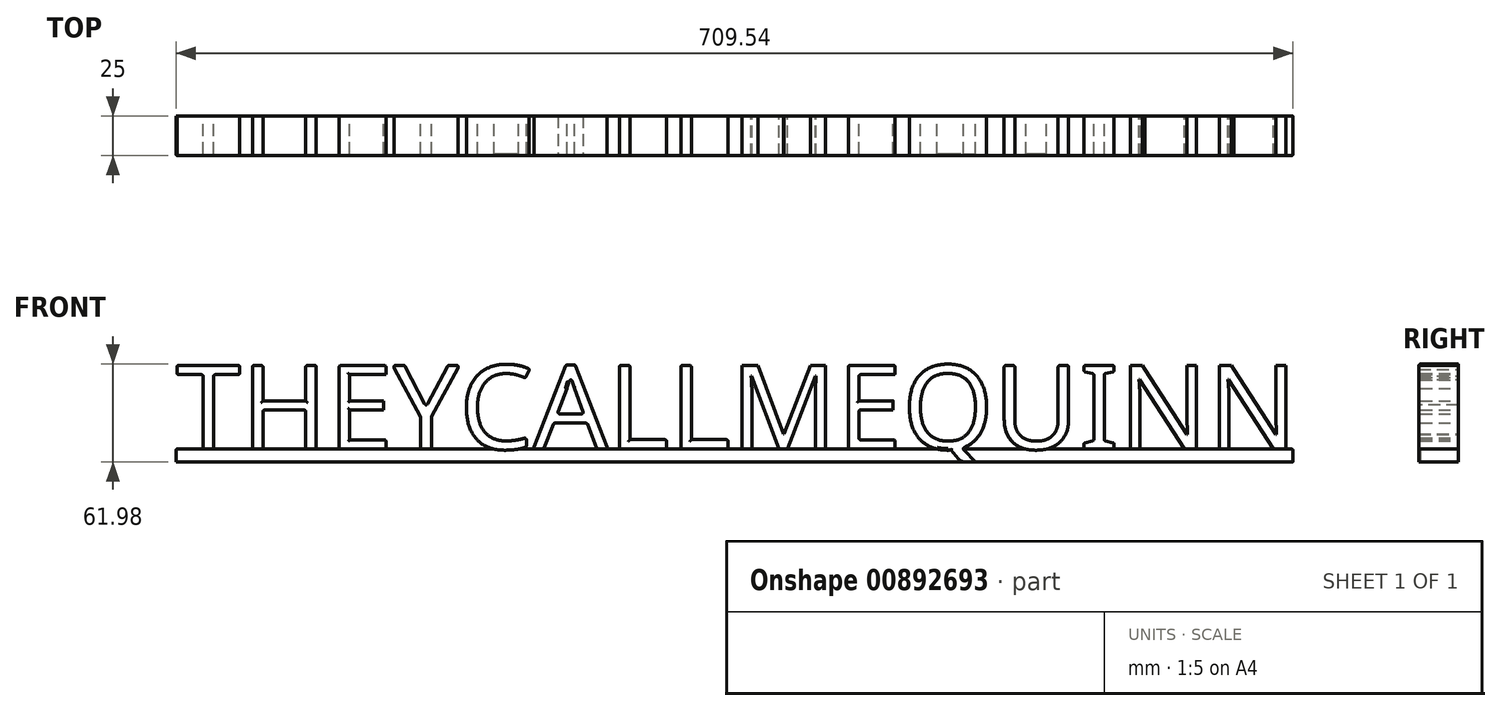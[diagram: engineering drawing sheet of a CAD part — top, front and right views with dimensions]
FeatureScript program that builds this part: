
annotation { "Feature Type Name" : "Feature", "Feature Type Description" : "" }
export const myFeature = defineFeature(function(context is Context, id is Id, definition is map)
    precondition{}
    {
        {
            var Q0;
            Q0=qCreatedBy(makeId("Front.planeOp"),FACE);
            var sketch = newSketch(context, id + "F0", { "sketchPlane" : qUnion([Q0])});
            skText(sketch, "E0", { "text": "THEYCALLMEQUINN", "fontName": "NotoSans-Regular.ttf"});
            skLineSegment(sketch, "E1.bottom", {"start": v(-74, 3.83) * mm, "end": v(635.54, 3.83) * mm});
            skLineSegment(sketch, "E1.top", {"start": v(-74, -4.21) * mm, "end": v(635.54, -4.21) * mm});
            skLineSegment(sketch, "E1.left", {"start": v(-74, 3.83) * mm, "end": v(-74, -4.21) * mm});
            skLineSegment(sketch, "E1.right", {"start": v(635.54, 3.83) * mm, "end": v(635.54, -4.21) * mm});
            const initialGuessF0  = {"E0": [-0.074, 0.00383, 1, 0, 0.05356]};
            skSetInitialGuess(sketch, initialGuessF0);
            skSolve(sketch);
        }
        {
            var Q0;
            {var subQ0=sQuery(id+"F0.wireOp",EDGE,"E0.sketch_text.stroke-1");Q0=makeQuery(id+"F0.imprint","IMPRINT",FACE,{"disambiguationData":[TD([[makeQuery(id+"F0.imprint","IMPRINT",EDGE,{"derivedFrom":subQ0}),-1.0]])]});}
            var Q1;
            {var subQ0=sQuery(id+"F0.wireOp",EDGE,"E0.sketch_text.stroke-21");Q1=makeQuery(id+"F0.imprint","IMPRINT",FACE,{"disambiguationData":[TD([[makeQuery(id+"F0.imprint","IMPRINT",EDGE,{"derivedFrom":subQ0}),-1.0]])]});}
            var Q2;
            Q2=makeQuery(id+"F0.imprint","IMPRINT",FACE,{"disambiguationData":[TD([[makeQuery(id+"F0.imprint","IMPRINT",EDGE,{"derivedFrom":sQuery(id+"F0.wireOp",EDGE,"E0.sketch_text.stroke-32")}),-1.0]])]});
            var Q3;
            Q3=makeQuery(id+"F0.imprint","IMPRINT",FACE,{"disambiguationData":[TD([[makeQuery(id+"F0.imprint","IMPRINT",EDGE,{"derivedFrom":sQuery(id+"F0.wireOp",EDGE,"E0.sketch_text.stroke-41")}),-1.0]])]});
            var Q4;
            {var subQ0=sQuery(id+"F0.wireOp",EDGE,"E0.sketch_text.stroke-70");Q4=makeQuery(id+"F0.imprint","IMPRINT",FACE,{"disambiguationData":[TD([[makeQuery(id+"F0.imprint","IMPRINT",EDGE,{"derivedFrom":subQ0}),-1.0]])]});}
            var Q5;
            {var subQ1=sQuery(id+"F0.wireOp",EDGE,"E0.sketch_text.stroke-76");Q5=makeQuery(id+"F0.imprint","IMPRINT",FACE,{"disambiguationData":[TD([[makeQuery(id+"F0.imprint","IMPRINT",EDGE,{"derivedFrom":subQ1}),-1.0]])]});}
            var Q6;
            {var subQ1=sQuery(id+"F0.wireOp",EDGE,"E0.sketch_text.stroke-101");Q6=makeQuery(id+"F0.imprint","IMPRINT",FACE,{"disambiguationData":[TD([[makeQuery(id+"F0.imprint","IMPRINT",EDGE,{"derivedFrom":subQ1}),-1.0]])]});}
            var Q7;
            Q7=makeQuery(id+"F0.imprint","IMPRINT",FACE,{"disambiguationData":[TD([[makeQuery(id+"F0.imprint","IMPRINT",EDGE,{"derivedFrom":sQuery(id+"F0.wireOp",EDGE,"E0.sketch_text.stroke-132")}),-1.0]])]});
            var Q8;
            {var subQ1=sQuery(id+"F0.wireOp",EDGE,"E0.sketch_text.stroke-147");Q8=makeQuery(id+"F0.imprint","IMPRINT",FACE,{"disambiguationData":[TD([[makeQuery(id+"F0.imprint","IMPRINT",EDGE,{"derivedFrom":subQ1}),-1.0]])]});}
            var Q9;
            {var subQ1=sQuery(id+"F0.wireOp",EDGE,"E0.sketch_text.stroke-9");Q9=makeQuery(id+"F0.imprint","IMPRINT",FACE,{"disambiguationData":[TD([[makeQuery(id+"F0.imprint","IMPRINT",EDGE,{"derivedFrom":subQ1}),-1.0]])]});}
            var Q10;
            {var subQ0=sQuery(id+"F0.wireOp",EDGE,"E0.sketch_text.stroke-48");Q10=makeQuery(id+"F0.imprint","IMPRINT",FACE,{"disambiguationData":[TD([[makeQuery(id+"F0.imprint","IMPRINT",EDGE,{"derivedFrom":subQ0}),-1.0]])]});}
            var Q11;
            Q11=makeQuery(id+"F0.imprint","IMPRINT",FACE,{"disambiguationData":[TD([[makeQuery(id+"F0.imprint","IMPRINT",EDGE,{"derivedFrom":sQuery(id+"F0.wireOp",EDGE,"E0.sketch_text.stroke-112")}),-1.0]])]});
            var Q12;
            {var subQ0=sQuery(id+"F0.wireOp",EDGE,"E0.sketch_text.stroke-135");var subQ1=sQuery(id+"F0.wireOp",EDGE,"E0.sketch_text.stroke-134");var subQ2=makeQuery(id+"F0.imprint","INTERSECT",VERTEX,{"derivedFrom":[subQ1,subQ0]});Q12=makeQuery(id+"F0.imprint","IMPRINT",FACE,{"disambiguationData":[TD([[makeQuery(id+"F0.imprint","IMPRINT",EDGE,{"disambiguationData":[TD([[subQ2,1.0]])],"derivedFrom":subQ1}),-1.0]])]});}
            var Q13;
            {var subQ2=sQuery(id+"F0.wireOp",EDGE,"E0.sketch_text.stroke-159");Q13=makeQuery(id+"F0.imprint","IMPRINT",FACE,{"disambiguationData":[TD([[makeQuery(id+"F0.imprint","IMPRINT",EDGE,{"derivedFrom":subQ2}),-1.0]])]});}
            var Q14;
            {var subQ3=sQuery(id+"F0.wireOp",EDGE,"E0.sketch_text.stroke-177");Q14=makeQuery(id+"F0.imprint","IMPRINT",FACE,{"disambiguationData":[TD([[makeQuery(id+"F0.imprint","IMPRINT",EDGE,{"derivedFrom":subQ3}),-1.0]])]});}
            var Q15;
            {var subQ1=sQuery(id+"F0.wireOp",EDGE,"E0.sketch_text.stroke-57");Q15=makeQuery(id+"F0.imprint","IMPRINT",FACE,{"disambiguationData":[TD([[makeQuery(id+"F0.imprint","IMPRINT",EDGE,{"derivedFrom":subQ1}),-1.0]])]});}
            var Q16;
            {var subQ1=sQuery(id+"F0.wireOp",EDGE,"E0.sketch_text.stroke-82");Q16=makeQuery(id+"F0.imprint","IMPRINT",FACE,{"disambiguationData":[TD([[makeQuery(id+"F0.imprint","IMPRINT",EDGE,{"derivedFrom":subQ1}),-1.0]])]});}
            var Q17;
            {var subQ1=sQuery(id+"F0.wireOp",EDGE,"E0.sketch_text.stroke-117");Q17=makeQuery(id+"F0.imprint","IMPRINT",FACE,{"disambiguationData":[TD([[makeQuery(id+"F0.imprint","IMPRINT",EDGE,{"derivedFrom":subQ1}),-1.0]])]});}
            extrude(context, id + "F1", {"entities" : qUnion([Q0, Q1, Q2, Q3, Q4, Q5, Q6, Q7, Q8, Q9, Q10, Q11, Q12, Q13, Q14, Q15, Q16, Q17]), "depth" : 25 * mm, "offsetDistance" : 25 * mm});
        }
        {
            var Q0;
            Q0=makeQuery(id+"F1.opExtrude","CAP_FACE",FACE,{"disambiguationData":[OSD([sQuery(id+"F0.wireOp",EDGE,"E0.sketch_text.stroke-1"),sQuery(id+"F0.wireOp",EDGE,"E0.sketch_text.stroke-2"),sQuery(id+"F0.wireOp",EDGE,"E0.sketch_text.stroke-3"),sQuery(id+"F0.wireOp",EDGE,"E0.sketch_text.stroke-4"),sQuery(id+"F0.wireOp",EDGE,"E0.sketch_text.stroke-5"),sQuery(id+"F0.wireOp",EDGE,"E0.sketch_text.stroke-6"),sQuery(id+"F0.wireOp",EDGE,"E0.sketch_text.stroke-7"),sQuery(id+"F0.wireOp",EDGE,"E1.bottom")])],"isStart":false});
            var Q1;
            Q1=makeQuery(id+"F1.opExtrude","CAP_FACE",FACE,{"disambiguationData":[OSD([sQuery(id+"F0.wireOp",EDGE,"E0.sketch_text.stroke-9"),sQuery(id+"F0.wireOp",EDGE,"E0.sketch_text.stroke-10"),sQuery(id+"F0.wireOp",EDGE,"E0.sketch_text.stroke-11"),sQuery(id+"F0.wireOp",EDGE,"E0.sketch_text.stroke-13"),sQuery(id+"F0.wireOp",EDGE,"E0.sketch_text.stroke-14"),sQuery(id+"F0.wireOp",EDGE,"E0.sketch_text.stroke-15"),sQuery(id+"F0.wireOp",EDGE,"E0.sketch_text.stroke-16"),sQuery(id+"F0.wireOp",EDGE,"E0.sketch_text.stroke-17"),sQuery(id+"F0.wireOp",EDGE,"E0.sketch_text.stroke-18"),sQuery(id+"F0.wireOp",EDGE,"E0.sketch_text.stroke-19"),sQuery(id+"F0.wireOp",EDGE,"E1.bottom")])],"isStart":false});
            var Q2;
            Q2=makeQuery(id+"F1.opExtrude","CAP_FACE",FACE,{"disambiguationData":[OSD([sQuery(id+"F0.wireOp",EDGE,"E0.sketch_text.stroke-21"),sQuery(id+"F0.wireOp",EDGE,"E0.sketch_text.stroke-22"),sQuery(id+"F0.wireOp",EDGE,"E0.sketch_text.stroke-23"),sQuery(id+"F0.wireOp",EDGE,"E0.sketch_text.stroke-24"),sQuery(id+"F0.wireOp",EDGE,"E0.sketch_text.stroke-25"),sQuery(id+"F0.wireOp",EDGE,"E0.sketch_text.stroke-26"),sQuery(id+"F0.wireOp",EDGE,"E0.sketch_text.stroke-27"),sQuery(id+"F0.wireOp",EDGE,"E0.sketch_text.stroke-28"),sQuery(id+"F0.wireOp",EDGE,"E0.sketch_text.stroke-29"),sQuery(id+"F0.wireOp",EDGE,"E0.sketch_text.stroke-30"),sQuery(id+"F0.wireOp",EDGE,"E0.sketch_text.stroke-31"),sQuery(id+"F0.wireOp",EDGE,"E1.bottom")])],"isStart":false});
            var Q3;
            Q3=makeQuery(id+"F1.opExtrude","CAP_FACE",FACE,{"disambiguationData":[OSD([sQuery(id+"F0.wireOp",EDGE,"E0.sketch_text.stroke-32"),sQuery(id+"F0.wireOp",EDGE,"E0.sketch_text.stroke-33"),sQuery(id+"F0.wireOp",EDGE,"E0.sketch_text.stroke-34"),sQuery(id+"F0.wireOp",EDGE,"E0.sketch_text.stroke-35"),sQuery(id+"F0.wireOp",EDGE,"E0.sketch_text.stroke-37"),sQuery(id+"F0.wireOp",EDGE,"E0.sketch_text.stroke-38"),sQuery(id+"F0.wireOp",EDGE,"E0.sketch_text.stroke-39"),sQuery(id+"F0.wireOp",EDGE,"E0.sketch_text.stroke-40"),sQuery(id+"F0.wireOp",EDGE,"E1.bottom")])],"isStart":false});
            var Q4;
            Q4=makeQuery(id+"F1.opExtrude","CAP_FACE",FACE,{"disambiguationData":[OSD([sQuery(id+"F0.wireOp",EDGE,"E0.sketch_text.stroke-41"),sQuery(id+"F0.wireOp",EDGE,"E0.sketch_text.stroke-42"),sQuery(id+"F0.wireOp",EDGE,"E0.sketch_text.stroke-43"),sQuery(id+"F0.wireOp",EDGE,"E0.sketch_text.stroke-44"),sQuery(id+"F0.wireOp",EDGE,"E0.sketch_text.stroke-45"),sQuery(id+"F0.wireOp",EDGE,"E0.sketch_text.stroke-46"),sQuery(id+"F0.wireOp",EDGE,"E0.sketch_text.stroke-47"),sQuery(id+"F0.wireOp",EDGE,"E0.sketch_text.stroke-48"),sQuery(id+"F0.wireOp",EDGE,"E0.sketch_text.stroke-49"),sQuery(id+"F0.wireOp",EDGE,"E0.sketch_text.stroke-50"),sQuery(id+"F0.wireOp",EDGE,"E0.sketch_text.stroke-51"),sQuery(id+"F0.wireOp",EDGE,"E0.sketch_text.stroke-52"),sQuery(id+"F0.wireOp",EDGE,"E0.sketch_text.stroke-53"),sQuery(id+"F0.wireOp",EDGE,"E0.sketch_text.stroke-54"),sQuery(id+"F0.wireOp",EDGE,"E0.sketch_text.stroke-55"),sQuery(id+"F0.wireOp",EDGE,"E0.sketch_text.stroke-56")])],"isStart":false});
            var Q5;
            Q5=makeQuery(id+"F1.opExtrude","CAP_FACE",FACE,{"disambiguationData":[OSD([sQuery(id+"F0.wireOp",EDGE,"E0.sketch_text.stroke-57"),sQuery(id+"F0.wireOp",EDGE,"E0.sketch_text.stroke-58"),sQuery(id+"F0.wireOp",EDGE,"E0.sketch_text.stroke-59"),sQuery(id+"F0.wireOp",EDGE,"E0.sketch_text.stroke-61"),sQuery(id+"F0.wireOp",EDGE,"E0.sketch_text.stroke-62"),sQuery(id+"F0.wireOp",EDGE,"E0.sketch_text.stroke-63"),sQuery(id+"F0.wireOp",EDGE,"E0.sketch_text.stroke-65"),sQuery(id+"F0.wireOp",EDGE,"E0.sketch_text.stroke-66"),sQuery(id+"F0.wireOp",EDGE,"E0.sketch_text.stroke-67"),sQuery(id+"F0.wireOp",EDGE,"E0.sketch_text.stroke-68"),sQuery(id+"F0.wireOp",EDGE,"E0.sketch_text.stroke-69"),sQuery(id+"F0.wireOp",EDGE,"E1.bottom")])],"isStart":false});
            var Q6;
            Q6=makeQuery(id+"F1.opExtrude","CAP_FACE",FACE,{"disambiguationData":[OSD([sQuery(id+"F0.wireOp",EDGE,"E0.sketch_text.stroke-70"),sQuery(id+"F0.wireOp",EDGE,"E0.sketch_text.stroke-71"),sQuery(id+"F0.wireOp",EDGE,"E0.sketch_text.stroke-72"),sQuery(id+"F0.wireOp",EDGE,"E0.sketch_text.stroke-73"),sQuery(id+"F0.wireOp",EDGE,"E0.sketch_text.stroke-74"),sQuery(id+"F0.wireOp",EDGE,"E1.bottom")])],"isStart":false});
            var Q7;
            Q7=makeQuery(id+"F1.opExtrude","CAP_FACE",FACE,{"disambiguationData":[OSD([sQuery(id+"F0.wireOp",EDGE,"E0.sketch_text.stroke-76"),sQuery(id+"F0.wireOp",EDGE,"E0.sketch_text.stroke-77"),sQuery(id+"F0.wireOp",EDGE,"E0.sketch_text.stroke-78"),sQuery(id+"F0.wireOp",EDGE,"E0.sketch_text.stroke-79"),sQuery(id+"F0.wireOp",EDGE,"E0.sketch_text.stroke-80"),sQuery(id+"F0.wireOp",EDGE,"E1.bottom")])],"isStart":false});
            var Q8;
            Q8=makeQuery(id+"F1.opExtrude","CAP_FACE",FACE,{"disambiguationData":[OSD([sQuery(id+"F0.wireOp",EDGE,"E0.sketch_text.stroke-82"),sQuery(id+"F0.wireOp",EDGE,"E0.sketch_text.stroke-83"),sQuery(id+"F0.wireOp",EDGE,"E0.sketch_text.stroke-84"),sQuery(id+"F0.wireOp",EDGE,"E0.sketch_text.stroke-85"),sQuery(id+"F0.wireOp",EDGE,"E0.sketch_text.stroke-87"),sQuery(id+"F0.wireOp",EDGE,"E0.sketch_text.stroke-88"),sQuery(id+"F0.wireOp",EDGE,"E0.sketch_text.stroke-89"),sQuery(id+"F0.wireOp",EDGE,"E0.sketch_text.stroke-90"),sQuery(id+"F0.wireOp",EDGE,"E0.sketch_text.stroke-91"),sQuery(id+"F0.wireOp",EDGE,"E0.sketch_text.stroke-92"),sQuery(id+"F0.wireOp",EDGE,"E0.sketch_text.stroke-93"),sQuery(id+"F0.wireOp",EDGE,"E0.sketch_text.stroke-95"),sQuery(id+"F0.wireOp",EDGE,"E0.sketch_text.stroke-96"),sQuery(id+"F0.wireOp",EDGE,"E0.sketch_text.stroke-97"),sQuery(id+"F0.wireOp",EDGE,"E0.sketch_text.stroke-98"),sQuery(id+"F0.wireOp",EDGE,"E1.bottom")])],"isStart":false});
            var Q9;
            Q9=makeQuery(id+"F1.opExtrude","CAP_FACE",FACE,{"disambiguationData":[OSD([sQuery(id+"F0.wireOp",EDGE,"E0.sketch_text.stroke-101"),sQuery(id+"F0.wireOp",EDGE,"E0.sketch_text.stroke-102"),sQuery(id+"F0.wireOp",EDGE,"E0.sketch_text.stroke-103"),sQuery(id+"F0.wireOp",EDGE,"E0.sketch_text.stroke-104"),sQuery(id+"F0.wireOp",EDGE,"E0.sketch_text.stroke-105"),sQuery(id+"F0.wireOp",EDGE,"E0.sketch_text.stroke-106"),sQuery(id+"F0.wireOp",EDGE,"E0.sketch_text.stroke-107"),sQuery(id+"F0.wireOp",EDGE,"E0.sketch_text.stroke-108"),sQuery(id+"F0.wireOp",EDGE,"E0.sketch_text.stroke-109"),sQuery(id+"F0.wireOp",EDGE,"E0.sketch_text.stroke-110"),sQuery(id+"F0.wireOp",EDGE,"E0.sketch_text.stroke-111"),sQuery(id+"F0.wireOp",EDGE,"E1.bottom")])],"isStart":false});
            var Q10;
            Q10=makeQuery(id+"F1.opExtrude","CAP_FACE",FACE,{"disambiguationData":[OSD([sQuery(id+"F0.wireOp",EDGE,"E0.sketch_text.stroke-112"),sQuery(id+"F0.wireOp",EDGE,"E0.sketch_text.stroke-113"),sQuery(id+"F0.wireOp",EDGE,"E0.sketch_text.stroke-114"),sQuery(id+"F0.wireOp",EDGE,"E0.sketch_text.stroke-116"),sQuery(id+"F0.wireOp",EDGE,"E0.sketch_text.stroke-117"),sQuery(id+"F0.wireOp",EDGE,"E0.sketch_text.stroke-118"),sQuery(id+"F0.wireOp",EDGE,"E0.sketch_text.stroke-119"),sQuery(id+"F0.wireOp",EDGE,"E0.sketch_text.stroke-120"),sQuery(id+"F0.wireOp",EDGE,"E0.sketch_text.stroke-121"),sQuery(id+"F0.wireOp",EDGE,"E0.sketch_text.stroke-122"),sQuery(id+"F0.wireOp",EDGE,"E0.sketch_text.stroke-123"),sQuery(id+"F0.wireOp",EDGE,"E0.sketch_text.stroke-124"),sQuery(id+"F0.wireOp",EDGE,"E0.sketch_text.stroke-125"),sQuery(id+"F0.wireOp",EDGE,"E0.sketch_text.stroke-126"),sQuery(id+"F0.wireOp",EDGE,"E0.sketch_text.stroke-127"),sQuery(id+"F0.wireOp",EDGE,"E0.sketch_text.stroke-128"),sQuery(id+"F0.wireOp",EDGE,"E0.sketch_text.stroke-129"),sQuery(id+"F0.wireOp",EDGE,"E0.sketch_text.stroke-130"),sQuery(id+"F0.wireOp",EDGE,"E0.sketch_text.stroke-131"),sQuery(id+"F0.wireOp",EDGE,"E1.top")])],"isStart":false});
            var Q11;
            Q11=makeQuery(id+"F1.opExtrude","CAP_EDGE",EDGE,{"disambiguationData":[OSD([sQuery(id+"F0.wireOp",EDGE,"E0.sketch_text.stroke-141")])],"isStart":false});
            var Q12;
            Q12=makeQuery(id+"F1.opExtrude","CAP_FACE",FACE,{"disambiguationData":[OSD([sQuery(id+"F0.wireOp",EDGE,"E0.sketch_text.stroke-132"),sQuery(id+"F0.wireOp",EDGE,"E0.sketch_text.stroke-133"),sQuery(id+"F0.wireOp",EDGE,"E0.sketch_text.stroke-134"),sQuery(id+"F0.wireOp",EDGE,"E0.sketch_text.stroke-135"),sQuery(id+"F0.wireOp",EDGE,"E0.sketch_text.stroke-136"),sQuery(id+"F0.wireOp",EDGE,"E0.sketch_text.stroke-137"),sQuery(id+"F0.wireOp",EDGE,"E0.sketch_text.stroke-138"),sQuery(id+"F0.wireOp",EDGE,"E0.sketch_text.stroke-139"),sQuery(id+"F0.wireOp",EDGE,"E0.sketch_text.stroke-140"),sQuery(id+"F0.wireOp",EDGE,"E0.sketch_text.stroke-141"),sQuery(id+"F0.wireOp",EDGE,"E0.sketch_text.stroke-142"),sQuery(id+"F0.wireOp",EDGE,"E0.sketch_text.stroke-143"),sQuery(id+"F0.wireOp",EDGE,"E0.sketch_text.stroke-144"),sQuery(id+"F0.wireOp",EDGE,"E0.sketch_text.stroke-145")])],"isStart":false});
            var Q13;
            Q13=makeQuery(id+"F1.opExtrude","CAP_FACE",FACE,{"disambiguationData":[OSD([sQuery(id+"F0.wireOp",EDGE,"E0.sketch_text.stroke-147"),sQuery(id+"F0.wireOp",EDGE,"E0.sketch_text.stroke-148"),sQuery(id+"F0.wireOp",EDGE,"E0.sketch_text.stroke-149"),sQuery(id+"F0.wireOp",EDGE,"E0.sketch_text.stroke-150"),sQuery(id+"F0.wireOp",EDGE,"E0.sketch_text.stroke-151"),sQuery(id+"F0.wireOp",EDGE,"E0.sketch_text.stroke-152"),sQuery(id+"F0.wireOp",EDGE,"E0.sketch_text.stroke-153"),sQuery(id+"F0.wireOp",EDGE,"E0.sketch_text.stroke-154"),sQuery(id+"F0.wireOp",EDGE,"E0.sketch_text.stroke-155"),sQuery(id+"F0.wireOp",EDGE,"E0.sketch_text.stroke-156"),sQuery(id+"F0.wireOp",EDGE,"E0.sketch_text.stroke-157"),sQuery(id+"F0.wireOp",EDGE,"E1.bottom")])],"isStart":false});
            var Q14;
            Q14=makeQuery(id+"F1.opExtrude","CAP_FACE",FACE,{"disambiguationData":[OSD([sQuery(id+"F0.wireOp",EDGE,"E0.sketch_text.stroke-159"),sQuery(id+"F0.wireOp",EDGE,"E0.sketch_text.stroke-160"),sQuery(id+"F0.wireOp",EDGE,"E0.sketch_text.stroke-161"),sQuery(id+"F0.wireOp",EDGE,"E0.sketch_text.stroke-162"),sQuery(id+"F0.wireOp",EDGE,"E0.sketch_text.stroke-163"),sQuery(id+"F0.wireOp",EDGE,"E0.sketch_text.stroke-165"),sQuery(id+"F0.wireOp",EDGE,"E0.sketch_text.stroke-166"),sQuery(id+"F0.wireOp",EDGE,"E0.sketch_text.stroke-167"),sQuery(id+"F0.wireOp",EDGE,"E0.sketch_text.stroke-168"),sQuery(id+"F0.wireOp",EDGE,"E0.sketch_text.stroke-169"),sQuery(id+"F0.wireOp",EDGE,"E0.sketch_text.stroke-170"),sQuery(id+"F0.wireOp",EDGE,"E0.sketch_text.stroke-171"),sQuery(id+"F0.wireOp",EDGE,"E0.sketch_text.stroke-172"),sQuery(id+"F0.wireOp",EDGE,"E0.sketch_text.stroke-173"),sQuery(id+"F0.wireOp",EDGE,"E0.sketch_text.stroke-174"),sQuery(id+"F0.wireOp",EDGE,"E0.sketch_text.stroke-175"),sQuery(id+"F0.wireOp",EDGE,"E1.bottom")])],"isStart":false});
            var Q15;
            Q15=makeQuery(id+"F1.opExtrude","CAP_FACE",FACE,{"disambiguationData":[OSD([sQuery(id+"F0.wireOp",EDGE,"E0.sketch_text.stroke-177"),sQuery(id+"F0.wireOp",EDGE,"E0.sketch_text.stroke-178"),sQuery(id+"F0.wireOp",EDGE,"E0.sketch_text.stroke-179"),sQuery(id+"F0.wireOp",EDGE,"E0.sketch_text.stroke-180"),sQuery(id+"F0.wireOp",EDGE,"E0.sketch_text.stroke-181"),sQuery(id+"F0.wireOp",EDGE,"E0.sketch_text.stroke-183"),sQuery(id+"F0.wireOp",EDGE,"E0.sketch_text.stroke-184"),sQuery(id+"F0.wireOp",EDGE,"E0.sketch_text.stroke-185"),sQuery(id+"F0.wireOp",EDGE,"E0.sketch_text.stroke-186"),sQuery(id+"F0.wireOp",EDGE,"E0.sketch_text.stroke-187"),sQuery(id+"F0.wireOp",EDGE,"E0.sketch_text.stroke-188"),sQuery(id+"F0.wireOp",EDGE,"E0.sketch_text.stroke-189"),sQuery(id+"F0.wireOp",EDGE,"E0.sketch_text.stroke-190"),sQuery(id+"F0.wireOp",EDGE,"E0.sketch_text.stroke-191"),sQuery(id+"F0.wireOp",EDGE,"E0.sketch_text.stroke-192"),sQuery(id+"F0.wireOp",EDGE,"E0.sketch_text.stroke-193"),sQuery(id+"F0.wireOp",EDGE,"E1.bottom")])],"isStart":false});
            var Q16;
            Q16=makeQuery(id+"F1.opExtrude","SWEPT_EDGE",EDGE,{"disambiguationData":[OSD([sQuery(id+"F0.wireOp",EDGE,"E0.sketch_text.stroke-3"),sQuery(id+"F0.wireOp",EDGE,"E0.sketch_text.stroke-4")])]});
            var Q17;
            Q17=makeQuery(id+"F1.opExtrude","SWEPT_EDGE",EDGE,{"disambiguationData":[OSD([sQuery(id+"F0.wireOp",EDGE,"E0.sketch_text.stroke-2"),sQuery(id+"F0.wireOp",EDGE,"E0.sketch_text.stroke-3")])]});
            var Q18;
            Q18=makeQuery(id+"F1.opExtrude","SWEPT_EDGE",EDGE,{"disambiguationData":[OSD([sQuery(id+"F0.wireOp",EDGE,"E0.sketch_text.stroke-1"),sQuery(id+"F0.wireOp",EDGE,"E0.sketch_text.stroke-2")])]});
            var Q19;
            Q19=makeQuery(id+"F1.opExtrude","SWEPT_EDGE",EDGE,{"disambiguationData":[OSD([sQuery(id+"F0.wireOp",EDGE,"E0.sketch_text.stroke-6"),sQuery(id+"F0.wireOp",EDGE,"E0.sketch_text.stroke-7")])]});
            var Q20;
            Q20=makeQuery(id+"F1.opExtrude","SWEPT_EDGE",EDGE,{"disambiguationData":[OSD([sQuery(id+"F0.wireOp",EDGE,"E0.sketch_text.stroke-5"),sQuery(id+"F0.wireOp",EDGE,"E0.sketch_text.stroke-6")])]});
            var Q21;
            Q21=makeQuery(id+"F1.opExtrude","SWEPT_EDGE",EDGE,{"disambiguationData":[OSD([sQuery(id+"F0.wireOp",EDGE,"E0.sketch_text.stroke-4"),sQuery(id+"F0.wireOp",EDGE,"E0.sketch_text.stroke-5")])]});
            var Q22;
            Q22=makeQuery(id+"F1.opExtrude","SWEPT_EDGE",EDGE,{"disambiguationData":[OSD([sQuery(id+"F0.wireOp",EDGE,"E0.sketch_text.stroke-14"),sQuery(id+"F0.wireOp",EDGE,"E0.sketch_text.stroke-15")])]});
            var Q23;
            Q23=makeQuery(id+"F1.opExtrude","SWEPT_EDGE",EDGE,{"disambiguationData":[OSD([sQuery(id+"F0.wireOp",EDGE,"E0.sketch_text.stroke-13"),sQuery(id+"F0.wireOp",EDGE,"E0.sketch_text.stroke-14")])]});
            var Q24;
            Q24=makeQuery(id+"F1.opExtrude","SWEPT_EDGE",EDGE,{"disambiguationData":[OSD([sQuery(id+"F0.wireOp",EDGE,"E0.sketch_text.stroke-17"),sQuery(id+"F0.wireOp",EDGE,"E0.sketch_text.stroke-18")])]});
            var Q25;
            Q25=makeQuery(id+"F1.opExtrude","SWEPT_EDGE",EDGE,{"disambiguationData":[OSD([sQuery(id+"F0.wireOp",EDGE,"E0.sketch_text.stroke-18"),sQuery(id+"F0.wireOp",EDGE,"E0.sketch_text.stroke-19")])]});
            var Q26;
            Q26=makeQuery(id+"F1.opExtrude","SWEPT_EDGE",EDGE,{"disambiguationData":[OSD([sQuery(id+"F0.wireOp",EDGE,"E0.sketch_text.stroke-11"),sQuery(id+"F0.wireOp",EDGE,"E1.bottom")])]});
            var Q27;
            Q27=makeQuery(id+"F1.opExtrude","SWEPT_EDGE",EDGE,{"disambiguationData":[OSD([sQuery(id+"F0.wireOp",EDGE,"E0.sketch_text.stroke-13"),sQuery(id+"F0.wireOp",EDGE,"E1.bottom")])]});
            var Q28;
            Q28=makeQuery(id+"F1.opExtrude","SWEPT_EDGE",EDGE,{"disambiguationData":[OSD([sQuery(id+"F0.wireOp",EDGE,"E0.sketch_text.stroke-7"),sQuery(id+"F0.wireOp",EDGE,"E1.bottom")])]});
            var Q29;
            Q29=makeQuery(id+"F1.opExtrude","SWEPT_EDGE",EDGE,{"disambiguationData":[OSD([sQuery(id+"F0.wireOp",EDGE,"E0.sketch_text.stroke-1"),sQuery(id+"F0.wireOp",EDGE,"E1.bottom")])]});
            var Q30;
            Q30=makeQuery(id+"F1.opExtrude","SWEPT_EDGE",EDGE,{"disambiguationData":[OSD([sQuery(id+"F0.wireOp",EDGE,"E0.sketch_text.stroke-9"),sQuery(id+"F0.wireOp",EDGE,"E1.bottom")])]});
            var Q31;
            Q31=makeQuery(id+"F1.opExtrude","SWEPT_EDGE",EDGE,{"disambiguationData":[OSD([sQuery(id+"F0.wireOp",EDGE,"E0.sketch_text.stroke-19"),sQuery(id+"F0.wireOp",EDGE,"E1.bottom")])]});
            var Q32;
            Q32=makeQuery(id+"F1.opExtrude","SWEPT_EDGE",EDGE,{"disambiguationData":[OSD([sQuery(id+"F0.wireOp",EDGE,"E0.sketch_text.stroke-21"),sQuery(id+"F0.wireOp",EDGE,"E1.bottom")])]});
            var Q33;
            Q33=makeQuery(id+"F1.opExtrude","SWEPT_EDGE",EDGE,{"disambiguationData":[OSD([sQuery(id+"F0.wireOp",EDGE,"E0.sketch_text.stroke-31"),sQuery(id+"F0.wireOp",EDGE,"E1.bottom")])]});
            var Q34;
            Q34=makeQuery(id+"F1.opExtrude","SWEPT_EDGE",EDGE,{"disambiguationData":[OSD([sQuery(id+"F0.wireOp",EDGE,"E0.sketch_text.stroke-21"),sQuery(id+"F0.wireOp",EDGE,"E0.sketch_text.stroke-22")])]});
            var Q35;
            Q35=makeQuery(id+"F1.opExtrude","SWEPT_EDGE",EDGE,{"disambiguationData":[OSD([sQuery(id+"F0.wireOp",EDGE,"E0.sketch_text.stroke-22"),sQuery(id+"F0.wireOp",EDGE,"E0.sketch_text.stroke-23")])]});
            var Q36;
            Q36=makeQuery(id+"F1.opExtrude","SWEPT_EDGE",EDGE,{"disambiguationData":[OSD([sQuery(id+"F0.wireOp",EDGE,"E0.sketch_text.stroke-38"),sQuery(id+"F0.wireOp",EDGE,"E0.sketch_text.stroke-39")])]});
            var Q37;
            Q37=makeQuery(id+"F1.opExtrude","SWEPT_EDGE",EDGE,{"disambiguationData":[OSD([sQuery(id+"F0.wireOp",EDGE,"E0.sketch_text.stroke-39"),sQuery(id+"F0.wireOp",EDGE,"E0.sketch_text.stroke-40")])]});
            var Q38;
            Q38=makeQuery(id+"F1.opExtrude","SWEPT_EDGE",EDGE,{"disambiguationData":[OSD([sQuery(id+"F0.wireOp",EDGE,"E0.sketch_text.stroke-32"),sQuery(id+"F0.wireOp",EDGE,"E0.sketch_text.stroke-33")])]});
            var Q39;
            Q39=makeQuery(id+"F1.opExtrude","SWEPT_EDGE",EDGE,{"disambiguationData":[OSD([sQuery(id+"F0.wireOp",EDGE,"E0.sketch_text.stroke-33"),sQuery(id+"F0.wireOp",EDGE,"E0.sketch_text.stroke-34")])]});
            var Q40;
            Q40=makeQuery(id+"F1.opExtrude","SWEPT_EDGE",EDGE,{"disambiguationData":[OSD([sQuery(id+"F0.wireOp",EDGE,"E0.sketch_text.stroke-32"),sQuery(id+"F0.wireOp",EDGE,"E0.sketch_text.stroke-40")])]});
            var Q41;
            Q41=makeQuery(id+"F1.opExtrude","SWEPT_EDGE",EDGE,{"disambiguationData":[OSD([sQuery(id+"F0.wireOp",EDGE,"E0.sketch_text.stroke-37"),sQuery(id+"F0.wireOp",EDGE,"E0.sketch_text.stroke-38")])]});
            var Q42;
            Q42=makeQuery(id+"F1.opExtrude","SWEPT_EDGE",EDGE,{"disambiguationData":[OSD([sQuery(id+"F0.wireOp",EDGE,"E0.sketch_text.stroke-34"),sQuery(id+"F0.wireOp",EDGE,"E0.sketch_text.stroke-35")])]});
            var Q43;
            Q43=makeQuery(id+"F1.opExtrude","SWEPT_EDGE",EDGE,{"disambiguationData":[OSD([sQuery(id+"F0.wireOp",EDGE,"E0.sketch_text.stroke-37"),sQuery(id+"F0.wireOp",EDGE,"E1.bottom")])]});
            var Q44;
            Q44=makeQuery(id+"F1.opExtrude","SWEPT_EDGE",EDGE,{"disambiguationData":[OSD([sQuery(id+"F0.wireOp",EDGE,"E0.sketch_text.stroke-35"),sQuery(id+"F0.wireOp",EDGE,"E1.bottom")])]});
            var Q45;
            Q45=makeQuery(id+"F1.opExtrude","SWEPT_EDGE",EDGE,{"disambiguationData":[OSD([sQuery(id+"F0.wireOp",EDGE,"E0.sketch_text.stroke-46"),sQuery(id+"F0.wireOp",EDGE,"E0.sketch_text.stroke-47")])]});
            var Q46;
            Q46=makeQuery(id+"F1.opExtrude","SWEPT_EDGE",EDGE,{"disambiguationData":[OSD([sQuery(id+"F0.wireOp",EDGE,"E0.sketch_text.stroke-45"),sQuery(id+"F0.wireOp",EDGE,"E0.sketch_text.stroke-46")])]});
            var Q47;
            Q47=makeQuery(id+"F1.opExtrude","SWEPT_EDGE",EDGE,{"disambiguationData":[OSD([sQuery(id+"F0.wireOp",EDGE,"E0.sketch_text.stroke-55"),sQuery(id+"F0.wireOp",EDGE,"E0.sketch_text.stroke-56")])]});
            var Q48;
            Q48=makeQuery(id+"F1.opExtrude","SWEPT_EDGE",EDGE,{"disambiguationData":[OSD([sQuery(id+"F0.wireOp",EDGE,"E0.sketch_text.stroke-54"),sQuery(id+"F0.wireOp",EDGE,"E0.sketch_text.stroke-55")])]});
            var Q49;
            Q49=makeQuery(id+"F1.opExtrude","SWEPT_EDGE",EDGE,{"disambiguationData":[OSD([sQuery(id+"F0.wireOp",EDGE,"E0.sketch_text.stroke-61"),sQuery(id+"F0.wireOp",EDGE,"E0.sketch_text.stroke-62")])]});
            var Q50;
            Q50=makeQuery(id+"F1.opExtrude","SWEPT_EDGE",EDGE,{"disambiguationData":[OSD([sQuery(id+"F0.wireOp",EDGE,"E0.sketch_text.stroke-62"),sQuery(id+"F0.wireOp",EDGE,"E0.sketch_text.stroke-63")])]});
            var Q51;
            Q51=makeQuery(id+"F1.opExtrude","SWEPT_EDGE",EDGE,{"disambiguationData":[OSD([sQuery(id+"F0.wireOp",EDGE,"E0.sketch_text.stroke-66"),sQuery(id+"F0.wireOp",EDGE,"E0.sketch_text.stroke-67")])]});
            var Q52;
            Q52=makeQuery(id+"F1.opExtrude","SWEPT_EDGE",EDGE,{"disambiguationData":[OSD([sQuery(id+"F0.wireOp",EDGE,"E0.sketch_text.stroke-68"),sQuery(id+"F0.wireOp",EDGE,"E0.sketch_text.stroke-69")])]});
            var Q53;
            Q53=makeQuery(id+"F1.opExtrude","SWEPT_EDGE",EDGE,{"disambiguationData":[OSD([sQuery(id+"F0.wireOp",EDGE,"E0.sketch_text.stroke-65"),sQuery(id+"F0.wireOp",EDGE,"E0.sketch_text.stroke-69")])]});
            var Q54;
            Q54=makeQuery(id+"F1.opExtrude","SWEPT_EDGE",EDGE,{"disambiguationData":[OSD([sQuery(id+"F0.wireOp",EDGE,"E0.sketch_text.stroke-58"),sQuery(id+"F0.wireOp",EDGE,"E0.sketch_text.stroke-59")])]});
            var Q55;
            Q55=makeQuery(id+"F1.opExtrude","SWEPT_EDGE",EDGE,{"disambiguationData":[OSD([sQuery(id+"F0.wireOp",EDGE,"E0.sketch_text.stroke-57"),sQuery(id+"F0.wireOp",EDGE,"E0.sketch_text.stroke-58")])]});
            var Q56;
            Q56=makeQuery(id+"F1.opExtrude","SWEPT_EDGE",EDGE,{"disambiguationData":[OSD([sQuery(id+"F0.wireOp",EDGE,"E0.sketch_text.stroke-57"),sQuery(id+"F0.wireOp",EDGE,"E1.bottom")])]});
            var Q57;
            Q57=makeQuery(id+"F1.opExtrude","SWEPT_EDGE",EDGE,{"disambiguationData":[OSD([sQuery(id+"F0.wireOp",EDGE,"E0.sketch_text.stroke-63"),sQuery(id+"F0.wireOp",EDGE,"E1.bottom")])]});
            var Q58;
            Q58=makeQuery(id+"F1.opExtrude","SWEPT_EDGE",EDGE,{"disambiguationData":[OSD([sQuery(id+"F0.wireOp",EDGE,"E0.sketch_text.stroke-59"),sQuery(id+"F0.wireOp",EDGE,"E1.bottom")])]});
            var Q59;
            Q59=makeQuery(id+"F1.opExtrude","SWEPT_EDGE",EDGE,{"disambiguationData":[OSD([sQuery(id+"F0.wireOp",EDGE,"E0.sketch_text.stroke-61"),sQuery(id+"F0.wireOp",EDGE,"E1.bottom")])]});
            var Q60;
            Q60=makeQuery(id+"F1.opExtrude","SWEPT_EDGE",EDGE,{"disambiguationData":[OSD([sQuery(id+"F0.wireOp",EDGE,"E0.sketch_text.stroke-70"),sQuery(id+"F0.wireOp",EDGE,"E1.bottom")])]});
            var Q61;
            Q61=makeQuery(id+"F1.opExtrude","SWEPT_EDGE",EDGE,{"disambiguationData":[OSD([sQuery(id+"F0.wireOp",EDGE,"E0.sketch_text.stroke-70"),sQuery(id+"F0.wireOp",EDGE,"E0.sketch_text.stroke-71")])]});
            var Q62;
            Q62=makeQuery(id+"F1.opExtrude","SWEPT_EDGE",EDGE,{"disambiguationData":[OSD([sQuery(id+"F0.wireOp",EDGE,"E0.sketch_text.stroke-74"),sQuery(id+"F0.wireOp",EDGE,"E1.bottom")])]});
            var Q63;
            Q63=makeQuery(id+"F1.opExtrude","SWEPT_EDGE",EDGE,{"disambiguationData":[OSD([sQuery(id+"F0.wireOp",EDGE,"E0.sketch_text.stroke-71"),sQuery(id+"F0.wireOp",EDGE,"E0.sketch_text.stroke-72")])]});
            var Q64;
            Q64=makeQuery(id+"F1.opExtrude","SWEPT_EDGE",EDGE,{"disambiguationData":[OSD([sQuery(id+"F0.wireOp",EDGE,"E0.sketch_text.stroke-76"),sQuery(id+"F0.wireOp",EDGE,"E1.bottom")])]});
            var Q65;
            Q65=makeQuery(id+"F1.opExtrude","SWEPT_EDGE",EDGE,{"disambiguationData":[OSD([sQuery(id+"F0.wireOp",EDGE,"E0.sketch_text.stroke-76"),sQuery(id+"F0.wireOp",EDGE,"E0.sketch_text.stroke-77")])]});
            var Q66;
            Q66=makeQuery(id+"F1.opExtrude","SWEPT_EDGE",EDGE,{"disambiguationData":[OSD([sQuery(id+"F0.wireOp",EDGE,"E0.sketch_text.stroke-80"),sQuery(id+"F0.wireOp",EDGE,"E1.bottom")])]});
            var Q67;
            Q67=makeQuery(id+"F1.opExtrude","SWEPT_EDGE",EDGE,{"disambiguationData":[OSD([sQuery(id+"F0.wireOp",EDGE,"E0.sketch_text.stroke-79"),sQuery(id+"F0.wireOp",EDGE,"E0.sketch_text.stroke-80")])]});
            var Q68;
            Q68=makeQuery(id+"F1.opExtrude","SWEPT_EDGE",EDGE,{"disambiguationData":[OSD([sQuery(id+"F0.wireOp",EDGE,"E0.sketch_text.stroke-77"),sQuery(id+"F0.wireOp",EDGE,"E0.sketch_text.stroke-78")])]});
            var Q69;
            Q69=makeQuery(id+"F1.opExtrude","SWEPT_EDGE",EDGE,{"disambiguationData":[OSD([sQuery(id+"F0.wireOp",EDGE,"E0.sketch_text.stroke-87"),sQuery(id+"F0.wireOp",EDGE,"E0.sketch_text.stroke-88")])]});
            var Q70;
            Q70=makeQuery(id+"F1.opExtrude","SWEPT_EDGE",EDGE,{"disambiguationData":[OSD([sQuery(id+"F0.wireOp",EDGE,"E0.sketch_text.stroke-88"),sQuery(id+"F0.wireOp",EDGE,"E0.sketch_text.stroke-89")])]});
            var Q71;
            Q71=makeQuery(id+"F1.opExtrude","SWEPT_EDGE",EDGE,{"disambiguationData":[OSD([sQuery(id+"F0.wireOp",EDGE,"E0.sketch_text.stroke-91"),sQuery(id+"F0.wireOp",EDGE,"E0.sketch_text.stroke-92")])]});
            var Q72;
            Q72=makeQuery(id+"F1.opExtrude","SWEPT_EDGE",EDGE,{"disambiguationData":[OSD([sQuery(id+"F0.wireOp",EDGE,"E0.sketch_text.stroke-92"),sQuery(id+"F0.wireOp",EDGE,"E0.sketch_text.stroke-93")])]});
            var Q73;
            Q73=makeQuery(id+"F1.opExtrude","SWEPT_EDGE",EDGE,{"disambiguationData":[OSD([sQuery(id+"F0.wireOp",EDGE,"E0.sketch_text.stroke-93"),sQuery(id+"F0.wireOp",EDGE,"E1.bottom")])]});
            var Q74;
            Q74=makeQuery(id+"F1.opExtrude","SWEPT_EDGE",EDGE,{"disambiguationData":[OSD([sQuery(id+"F0.wireOp",EDGE,"E0.sketch_text.stroke-95"),sQuery(id+"F0.wireOp",EDGE,"E1.bottom")])]});
            var Q75;
            Q75=makeQuery(id+"F1.opExtrude","SWEPT_EDGE",EDGE,{"disambiguationData":[OSD([sQuery(id+"F0.wireOp",EDGE,"E0.sketch_text.stroke-98"),sQuery(id+"F0.wireOp",EDGE,"E1.bottom")])]});
            var Q76;
            Q76=makeQuery(id+"F1.opExtrude","SWEPT_EDGE",EDGE,{"disambiguationData":[OSD([sQuery(id+"F0.wireOp",EDGE,"E0.sketch_text.stroke-82"),sQuery(id+"F0.wireOp",EDGE,"E1.bottom")])]});
            var Q77;
            Q77=makeQuery(id+"F1.opExtrude","SWEPT_EDGE",EDGE,{"disambiguationData":[OSD([sQuery(id+"F0.wireOp",EDGE,"E0.sketch_text.stroke-85"),sQuery(id+"F0.wireOp",EDGE,"E1.bottom")])]});
            var Q78;
            Q78=makeQuery(id+"F1.opExtrude","SWEPT_EDGE",EDGE,{"disambiguationData":[OSD([sQuery(id+"F0.wireOp",EDGE,"E0.sketch_text.stroke-87"),sQuery(id+"F0.wireOp",EDGE,"E1.bottom")])]});
            var Q79;
            Q79=makeQuery(id+"F1.opExtrude","SWEPT_EDGE",EDGE,{"disambiguationData":[OSD([sQuery(id+"F0.wireOp",EDGE,"E0.sketch_text.stroke-101"),sQuery(id+"F0.wireOp",EDGE,"E1.bottom")])]});
            var Q80;
            Q80=makeQuery(id+"F1.opExtrude","SWEPT_EDGE",EDGE,{"disambiguationData":[OSD([sQuery(id+"F0.wireOp",EDGE,"E0.sketch_text.stroke-101"),sQuery(id+"F0.wireOp",EDGE,"E0.sketch_text.stroke-102")])]});
            var Q81;
            Q81=makeQuery(id+"F1.opExtrude","SWEPT_EDGE",EDGE,{"disambiguationData":[OSD([sQuery(id+"F0.wireOp",EDGE,"E0.sketch_text.stroke-111"),sQuery(id+"F0.wireOp",EDGE,"E1.bottom")])]});
            var Q82;
            Q82=makeQuery(id+"F1.opExtrude","SWEPT_EDGE",EDGE,{"disambiguationData":[OSD([sQuery(id+"F0.wireOp",EDGE,"E0.sketch_text.stroke-108"),sQuery(id+"F0.wireOp",EDGE,"E0.sketch_text.stroke-109")])]});
            var Q83;
            Q83=makeQuery(id+"F1.opExtrude","SWEPT_EDGE",EDGE,{"disambiguationData":[OSD([sQuery(id+"F0.wireOp",EDGE,"E0.sketch_text.stroke-109"),sQuery(id+"F0.wireOp",EDGE,"E0.sketch_text.stroke-110")])]});
            var Q84;
            Q84=makeQuery(id+"F1.opExtrude","SWEPT_EDGE",EDGE,{"disambiguationData":[OSD([sQuery(id+"F0.wireOp",EDGE,"E0.sketch_text.stroke-104"),sQuery(id+"F0.wireOp",EDGE,"E0.sketch_text.stroke-105")])]});
            var Q85;
            Q85=makeQuery(id+"F1.opExtrude","SWEPT_EDGE",EDGE,{"disambiguationData":[OSD([sQuery(id+"F0.wireOp",EDGE,"E0.sketch_text.stroke-103"),sQuery(id+"F0.wireOp",EDGE,"E0.sketch_text.stroke-104")])]});
            var Q86;
            Q86=makeQuery(id+"F1.opExtrude","SWEPT_EDGE",EDGE,{"disambiguationData":[OSD([sQuery(id+"F0.wireOp",EDGE,"E0.sketch_text.stroke-102"),sQuery(id+"F0.wireOp",EDGE,"E0.sketch_text.stroke-103")])]});
            var Q87;
            Q87=makeQuery(id+"F1.opExtrude","SWEPT_EDGE",EDGE,{"disambiguationData":[OSD([sQuery(id+"F0.wireOp",EDGE,"E0.sketch_text.stroke-113"),sQuery(id+"F0.wireOp",EDGE,"E0.sketch_text.stroke-114")])]});
            var Q88;
            Q88=makeQuery(id+"F1.opExtrude","SWEPT_EDGE",EDGE,{"disambiguationData":[OSD([sQuery(id+"F0.wireOp",EDGE,"E0.sketch_text.stroke-138"),sQuery(id+"F0.wireOp",EDGE,"E0.sketch_text.stroke-139")])]});
            var Q89;
            Q89=makeQuery(id+"F1.opExtrude","SWEPT_EDGE",EDGE,{"disambiguationData":[OSD([sQuery(id+"F0.wireOp",EDGE,"E0.sketch_text.stroke-137"),sQuery(id+"F0.wireOp",EDGE,"E0.sketch_text.stroke-138")])]});
            var Q90;
            Q90=makeQuery(id+"F1.opExtrude","SWEPT_EDGE",EDGE,{"disambiguationData":[OSD([sQuery(id+"F0.wireOp",EDGE,"E0.sketch_text.stroke-144"),sQuery(id+"F0.wireOp",EDGE,"E0.sketch_text.stroke-145")])]});
            var Q91;
            Q91=makeQuery(id+"F1.opExtrude","SWEPT_EDGE",EDGE,{"disambiguationData":[OSD([sQuery(id+"F0.wireOp",EDGE,"E0.sketch_text.stroke-132"),sQuery(id+"F0.wireOp",EDGE,"E0.sketch_text.stroke-145")])]});
            var Q92;
            Q92=makeQuery(id+"F1.opExtrude","SWEPT_EDGE",EDGE,{"disambiguationData":[OSD([sQuery(id+"F0.wireOp",EDGE,"E0.sketch_text.stroke-151"),sQuery(id+"F0.wireOp",EDGE,"E0.sketch_text.stroke-152")])]});
            var Q93;
            Q93=makeQuery(id+"F1.opExtrude","SWEPT_EDGE",EDGE,{"disambiguationData":[OSD([sQuery(id+"F0.wireOp",EDGE,"E0.sketch_text.stroke-152"),sQuery(id+"F0.wireOp",EDGE,"E0.sketch_text.stroke-153")])]});
            var Q94;
            Q94=makeQuery(id+"F1.opExtrude","SWEPT_EDGE",EDGE,{"disambiguationData":[OSD([sQuery(id+"F0.wireOp",EDGE,"E0.sketch_text.stroke-153"),sQuery(id+"F0.wireOp",EDGE,"E0.sketch_text.stroke-154")])]});
            var Q95;
            Q95=makeQuery(id+"F1.opExtrude","SWEPT_EDGE",EDGE,{"disambiguationData":[OSD([sQuery(id+"F0.wireOp",EDGE,"E0.sketch_text.stroke-150"),sQuery(id+"F0.wireOp",EDGE,"E0.sketch_text.stroke-151")])]});
            var Q96;
            Q96=makeQuery(id+"F1.opExtrude","SWEPT_EDGE",EDGE,{"disambiguationData":[OSD([sQuery(id+"F0.wireOp",EDGE,"E0.sketch_text.stroke-149"),sQuery(id+"F0.wireOp",EDGE,"E0.sketch_text.stroke-150")])]});
            var Q97;
            Q97=makeQuery(id+"F1.opExtrude","SWEPT_EDGE",EDGE,{"disambiguationData":[OSD([sQuery(id+"F0.wireOp",EDGE,"E0.sketch_text.stroke-154"),sQuery(id+"F0.wireOp",EDGE,"E0.sketch_text.stroke-155")])]});
            var Q98;
            Q98=makeQuery(id+"F1.opExtrude","SWEPT_EDGE",EDGE,{"disambiguationData":[OSD([sQuery(id+"F0.wireOp",EDGE,"E0.sketch_text.stroke-148"),sQuery(id+"F0.wireOp",EDGE,"E0.sketch_text.stroke-149")])]});
            var Q99;
            Q99=makeQuery(id+"F1.opExtrude","SWEPT_EDGE",EDGE,{"disambiguationData":[OSD([sQuery(id+"F0.wireOp",EDGE,"E0.sketch_text.stroke-147"),sQuery(id+"F0.wireOp",EDGE,"E0.sketch_text.stroke-148")])]});
            var Q100;
            Q100=makeQuery(id+"F1.opExtrude","SWEPT_EDGE",EDGE,{"disambiguationData":[OSD([sQuery(id+"F0.wireOp",EDGE,"E0.sketch_text.stroke-147"),sQuery(id+"F0.wireOp",EDGE,"E1.bottom")])]});
            var Q101;
            Q101=makeQuery(id+"F1.opExtrude","SWEPT_EDGE",EDGE,{"disambiguationData":[OSD([sQuery(id+"F0.wireOp",EDGE,"E0.sketch_text.stroke-156"),sQuery(id+"F0.wireOp",EDGE,"E0.sketch_text.stroke-157")])]});
            var Q102;
            Q102=makeQuery(id+"F1.opExtrude","SWEPT_EDGE",EDGE,{"disambiguationData":[OSD([sQuery(id+"F0.wireOp",EDGE,"E0.sketch_text.stroke-157"),sQuery(id+"F0.wireOp",EDGE,"E1.bottom")])]});
            var Q103;
            Q103=makeQuery(id+"F1.opExtrude","SWEPT_EDGE",EDGE,{"disambiguationData":[OSD([sQuery(id+"F0.wireOp",EDGE,"E0.sketch_text.stroke-155"),sQuery(id+"F0.wireOp",EDGE,"E0.sketch_text.stroke-156")])]});
            var Q104;
            Q104=makeQuery(id+"F1.opExtrude","SWEPT_EDGE",EDGE,{"disambiguationData":[OSD([sQuery(id+"F0.wireOp",EDGE,"E0.sketch_text.stroke-166"),sQuery(id+"F0.wireOp",EDGE,"E0.sketch_text.stroke-167")])]});
            var Q105;
            Q105=makeQuery(id+"F1.opExtrude","SWEPT_EDGE",EDGE,{"disambiguationData":[OSD([sQuery(id+"F0.wireOp",EDGE,"E0.sketch_text.stroke-165"),sQuery(id+"F0.wireOp",EDGE,"E0.sketch_text.stroke-166")])]});
            var Q106;
            Q106=makeQuery(id+"F1.opExtrude","SWEPT_EDGE",EDGE,{"disambiguationData":[OSD([sQuery(id+"F0.wireOp",EDGE,"E0.sketch_text.stroke-173"),sQuery(id+"F0.wireOp",EDGE,"E0.sketch_text.stroke-174")])]});
            var Q107;
            Q107=makeQuery(id+"F1.opExtrude","SWEPT_EDGE",EDGE,{"disambiguationData":[OSD([sQuery(id+"F0.wireOp",EDGE,"E0.sketch_text.stroke-174"),sQuery(id+"F0.wireOp",EDGE,"E0.sketch_text.stroke-175")])]});
            var Q108;
            Q108=makeQuery(id+"F1.opExtrude","SWEPT_EDGE",EDGE,{"disambiguationData":[OSD([sQuery(id+"F0.wireOp",EDGE,"E0.sketch_text.stroke-165"),sQuery(id+"F0.wireOp",EDGE,"E1.bottom")])]});
            var Q109;
            Q109=makeQuery(id+"F1.opExtrude","SWEPT_EDGE",EDGE,{"disambiguationData":[OSD([sQuery(id+"F0.wireOp",EDGE,"E0.sketch_text.stroke-163"),sQuery(id+"F0.wireOp",EDGE,"E1.bottom")])]});
            var Q110;
            Q110=makeQuery(id+"F1.opExtrude","SWEPT_EDGE",EDGE,{"disambiguationData":[OSD([sQuery(id+"F0.wireOp",EDGE,"E0.sketch_text.stroke-159"),sQuery(id+"F0.wireOp",EDGE,"E1.bottom")])]});
            var Q111;
            Q111=makeQuery(id+"F1.opExtrude","SWEPT_EDGE",EDGE,{"disambiguationData":[OSD([sQuery(id+"F0.wireOp",EDGE,"E0.sketch_text.stroke-175"),sQuery(id+"F0.wireOp",EDGE,"E1.bottom")])]});
            var Q112;
            Q112=makeQuery(id+"F1.opExtrude","SWEPT_EDGE",EDGE,{"disambiguationData":[OSD([sQuery(id+"F0.wireOp",EDGE,"E0.sketch_text.stroke-181"),sQuery(id+"F0.wireOp",EDGE,"E1.bottom")])]});
            var Q113;
            Q113=makeQuery(id+"F1.opExtrude","SWEPT_EDGE",EDGE,{"disambiguationData":[OSD([sQuery(id+"F0.wireOp",EDGE,"E0.sketch_text.stroke-183"),sQuery(id+"F0.wireOp",EDGE,"E1.bottom")])]});
            var Q114;
            Q114=makeQuery(id+"F1.opExtrude","SWEPT_EDGE",EDGE,{"disambiguationData":[OSD([sQuery(id+"F0.wireOp",EDGE,"E0.sketch_text.stroke-177"),sQuery(id+"F0.wireOp",EDGE,"E1.bottom")])]});
            var Q115;
            Q115=makeQuery(id+"F1.opExtrude","SWEPT_EDGE",EDGE,{"disambiguationData":[OSD([sQuery(id+"F0.wireOp",EDGE,"E0.sketch_text.stroke-193"),sQuery(id+"F0.wireOp",EDGE,"E1.bottom")])]});
            var Q116;
            Q116=makeQuery(id+"F1.opExtrude","SWEPT_EDGE",EDGE,{"disambiguationData":[OSD([sQuery(id+"F0.wireOp",EDGE,"E0.sketch_text.stroke-192"),sQuery(id+"F0.wireOp",EDGE,"E0.sketch_text.stroke-193")])]});
            var Q117;
            Q117=makeQuery(id+"F1.opExtrude","SWEPT_EDGE",EDGE,{"disambiguationData":[OSD([sQuery(id+"F0.wireOp",EDGE,"E0.sketch_text.stroke-191"),sQuery(id+"F0.wireOp",EDGE,"E0.sketch_text.stroke-192")])]});
            var Q118;
            Q118=makeQuery(id+"F1.opExtrude","SWEPT_EDGE",EDGE,{"disambiguationData":[OSD([sQuery(id+"F0.wireOp",EDGE,"E0.sketch_text.stroke-184"),sQuery(id+"F0.wireOp",EDGE,"E0.sketch_text.stroke-185")])]});
            var Q119;
            Q119=makeQuery(id+"F1.opExtrude","SWEPT_EDGE",EDGE,{"disambiguationData":[OSD([sQuery(id+"F0.wireOp",EDGE,"E0.sketch_text.stroke-183"),sQuery(id+"F0.wireOp",EDGE,"E0.sketch_text.stroke-184")])]});
            fillet(context, id + "F2", {"entities" : qUnion([Q0, Q1, Q2, Q3, Q4, Q5, Q6, Q7, Q8, Q9, Q10, Q11, Q12, Q13, Q14, Q15, Q16, Q17, Q18, Q19, Q20, Q21, Q22, Q23, Q24, Q25, Q26, Q27, Q28, Q29, Q30, Q31, Q32, Q33, Q34, Q35, Q36, Q37, Q38, Q39, Q40, Q41, Q42, Q43, Q44, Q45, Q46, Q47, Q48, Q49, Q50, Q51, Q52, Q53, Q54, Q55, Q56, Q57, Q58, Q59, Q60, Q61, Q62, Q63, Q64, Q65, Q66, Q67, Q68, Q69, Q70, Q71, Q72, Q73, Q74, Q75, Q76, Q77, Q78, Q79, Q80, Q81, Q82, Q83, Q84, Q85, Q86, Q87, Q88, Q89, Q90, Q91, Q92, Q93, Q94, Q95, Q96, Q97, Q98, Q99, Q100, Q101, Q102, Q103, Q104, Q105, Q106, Q107, Q108, Q109, Q110, Q111, Q112, Q113, Q114, Q115, Q116, Q117, Q118, Q119]), "tangentPropagation" : true, "radius" : 1 * mm, "defaultsChanged" : false, "vertexSettings" : [], "allowEdgeOverflow" : false});
        }
        {
            var Q0;
            {var subQ16=sQuery(id+"F0.wireOp",EDGE,"E0.sketch_text.stroke-48");Q0=makeQuery(id+"F0.imprint","IMPRINT",FACE,{"disambiguationData":[TD([[makeQuery(id+"F0.imprint","IMPRINT",EDGE,{"derivedFrom":subQ16}),1.0]])]});}
            var Q1;
            {var subQ20=sQuery(id+"F0.wireOp",EDGE,"E1.right");Q1=makeQuery(id+"F0.imprint","IMPRINT",FACE,{"disambiguationData":[TD([[makeQuery(id+"F0.imprint","IMPRINT",EDGE,{"derivedFrom":subQ20}),-1.0]])]});}
            extrude(context, id + "F3", {"entities" : qUnion([Q0, Q1]), "operationType" : NewBodyOperationType.ADD, "depth" : 25 * mm, "offsetDistance" : 25 * mm});
        }
        {
            var Q0;
            {var subQ0=sQuery(id+"F0.wireOp",EDGE,"E1.bottom");var subQ1=makeQuery(id+"F0.imprint","INTERSECT",VERTEX,{"derivedFrom":[sQuery(id+"F0.wireOp",EDGE,"E0.sketch_text.stroke-35"),subQ0]});var subQ3=makeQuery(id+"F0.imprint","INTERSECT",VERTEX,{"derivedFrom":[sQuery(id+"F0.wireOp",EDGE,"E0.sketch_text.stroke-31"),subQ0]});var subQ4=makeQuery(id+"F0.imprint","INTERSECT",VERTEX,{"derivedFrom":[sQuery(id+"F0.wireOp",EDGE,"E0.sketch_text.stroke-21"),subQ0]});var subQ5=makeQuery(id+"F0.imprint","INTERSECT",VERTEX,{"derivedFrom":[sQuery(id+"F0.wireOp",EDGE,"E0.sketch_text.stroke-19"),subQ0]});var subQ6=makeQuery(id+"F0.imprint","INTERSECT",VERTEX,{"derivedFrom":[sQuery(id+"F0.wireOp",EDGE,"E0.sketch_text.stroke-9"),subQ0]});var subQ7=makeQuery(id+"F0.imprint","INTERSECT",VERTEX,{"derivedFrom":[sQuery(id+"F0.wireOp",EDGE,"E0.sketch_text.stroke-11"),subQ0]});var subQ9=makeQuery(id+"F0.imprint","INTERSECT",VERTEX,{"derivedFrom":[sQuery(id+"F0.wireOp",EDGE,"E0.sketch_text.stroke-7"),subQ0]});var subQ10=makeQuery(id+"F0.imprint","INTERSECT",VERTEX,{"derivedFrom":[sQuery(id+"F0.wireOp",EDGE,"E0.sketch_text.stroke-1"),subQ0]});Q0=makeQuery(id+"F3.opExtrude","CAP_EDGE",EDGE,{"disambiguationData":[OSD([subQ0]),TDD([makeQuery(id+"F0.imprint","IMPRINT",EDGE,{"disambiguationData":[TD([[subQ10,1.0]])],"derivedFrom":subQ0}),makeQuery(id+"F0.imprint","IMPRINT",EDGE,{"disambiguationData":[TD([[subQ10,-1.0]])],"derivedFrom":subQ0}),makeQuery(id+"F0.imprint","IMPRINT",EDGE,{"disambiguationData":[TD([[subQ9,-1.0]])],"derivedFrom":subQ0}),makeQuery(id+"F0.imprint","IMPRINT",EDGE,{"disambiguationData":[TD([[subQ7,1.0]])],"derivedFrom":subQ0}),makeQuery(id+"F0.imprint","IMPRINT",EDGE,{"disambiguationData":[TD([[subQ6,1.0]])],"derivedFrom":subQ0}),makeQuery(id+"F0.imprint","IMPRINT",EDGE,{"disambiguationData":[TD([[subQ6,-1.0]])],"derivedFrom":subQ0}),makeQuery(id+"F0.imprint","IMPRINT",EDGE,{"disambiguationData":[TD([[subQ5,-1.0]])],"derivedFrom":subQ0}),makeQuery(id+"F0.imprint","IMPRINT",EDGE,{"disambiguationData":[TD([[subQ4,-1.0]])],"derivedFrom":subQ0}),makeQuery(id+"F0.imprint","IMPRINT",EDGE,{"disambiguationData":[TD([[subQ3,-1.0]])],"derivedFrom":subQ0}),makeQuery(id+"F0.imprint","IMPRINT",EDGE,{"disambiguationData":[TD([[subQ1,1.0]])],"derivedFrom":subQ0}),makeQuery(id+"F0.imprint","IMPRINT",EDGE,{"disambiguationData":[TD([[subQ1,-1.0]])],"derivedFrom":subQ0})])],"isStart":false});}
            var Q1;
            {var subQ0=sQuery(id+"F0.wireOp",EDGE,"E1.bottom");var subQ1=makeQuery(id+"F0.imprint","INTERSECT",VERTEX,{"derivedFrom":[sQuery(id+"F0.wireOp",EDGE,"E0.sketch_text.stroke-111"),subQ0]});var subQ2=makeQuery(id+"F0.imprint","INTERSECT",VERTEX,{"derivedFrom":[sQuery(id+"F0.wireOp",EDGE,"E0.sketch_text.stroke-101"),subQ0]});var subQ3=makeQuery(id+"F0.imprint","INTERSECT",VERTEX,{"derivedFrom":[sQuery(id+"F0.wireOp",EDGE,"E0.sketch_text.stroke-93"),subQ0]});var subQ4=makeQuery(id+"F0.imprint","INTERSECT",VERTEX,{"derivedFrom":[sQuery(id+"F0.wireOp",EDGE,"E0.sketch_text.stroke-95"),subQ0]});var subQ6=makeQuery(id+"F0.imprint","INTERSECT",VERTEX,{"derivedFrom":[sQuery(id+"F0.wireOp",EDGE,"E0.sketch_text.stroke-82"),subQ0]});var subQ7=makeQuery(id+"F0.imprint","INTERSECT",VERTEX,{"derivedFrom":[sQuery(id+"F0.wireOp",EDGE,"E0.sketch_text.stroke-85"),subQ0]});var subQ9=makeQuery(id+"F0.imprint","INTERSECT",VERTEX,{"derivedFrom":[sQuery(id+"F0.wireOp",EDGE,"E0.sketch_text.stroke-80"),subQ0]});var subQ10=makeQuery(id+"F0.imprint","INTERSECT",VERTEX,{"derivedFrom":[sQuery(id+"F0.wireOp",EDGE,"E0.sketch_text.stroke-76"),subQ0]});var subQ11=makeQuery(id+"F0.imprint","INTERSECT",VERTEX,{"derivedFrom":[sQuery(id+"F0.wireOp",EDGE,"E0.sketch_text.stroke-74"),subQ0]});var subQ12=makeQuery(id+"F0.imprint","INTERSECT",VERTEX,{"derivedFrom":[sQuery(id+"F0.wireOp",EDGE,"E0.sketch_text.stroke-70"),subQ0]});var subQ13=makeQuery(id+"F0.imprint","INTERSECT",VERTEX,{"derivedFrom":[sQuery(id+"F0.wireOp",EDGE,"E0.sketch_text.stroke-63"),subQ0]});var subQ14=makeQuery(id+"F0.imprint","INTERSECT",VERTEX,{"derivedFrom":[sQuery(id+"F0.wireOp",EDGE,"E0.sketch_text.stroke-57"),subQ0]});var subQ15=makeQuery(id+"F0.imprint","INTERSECT",VERTEX,{"derivedFrom":[sQuery(id+"F0.wireOp",EDGE,"E0.sketch_text.stroke-59"),subQ0]});var subQ16=makeQuery(id+"F0.imprint","INTERSECT",VERTEX,{"derivedFrom":[sQuery(id+"F0.wireOp",EDGE,"E0.sketch_text.stroke-61"),subQ0]});Q1=makeQuery(id+"F3.opExtrude","CAP_EDGE",EDGE,{"disambiguationData":[OSD([subQ0]),TDD([makeQuery(id+"F0.imprint","IMPRINT",EDGE,{"disambiguationData":[TD([[subQ16,1.0]])],"derivedFrom":subQ0}),makeQuery(id+"F0.imprint","IMPRINT",EDGE,{"disambiguationData":[TD([[subQ15,1.0]])],"derivedFrom":subQ0}),makeQuery(id+"F0.imprint","IMPRINT",EDGE,{"disambiguationData":[TD([[subQ14,1.0]])],"derivedFrom":subQ0}),makeQuery(id+"F0.imprint","IMPRINT",EDGE,{"disambiguationData":[TD([[subQ14,-1.0]])],"derivedFrom":subQ0}),makeQuery(id+"F0.imprint","IMPRINT",EDGE,{"disambiguationData":[TD([[subQ13,-1.0]])],"derivedFrom":subQ0}),makeQuery(id+"F0.imprint","IMPRINT",EDGE,{"disambiguationData":[TD([[subQ12,-1.0]])],"derivedFrom":subQ0}),makeQuery(id+"F0.imprint","IMPRINT",EDGE,{"disambiguationData":[TD([[subQ11,-1.0]])],"derivedFrom":subQ0}),makeQuery(id+"F0.imprint","IMPRINT",EDGE,{"disambiguationData":[TD([[subQ10,-1.0]])],"derivedFrom":subQ0}),makeQuery(id+"F0.imprint","IMPRINT",EDGE,{"disambiguationData":[TD([[subQ9,-1.0]])],"derivedFrom":subQ0}),makeQuery(id+"F0.imprint","IMPRINT",EDGE,{"disambiguationData":[TD([[subQ7,1.0]])],"derivedFrom":subQ0}),makeQuery(id+"F0.imprint","IMPRINT",EDGE,{"disambiguationData":[TD([[subQ6,1.0]])],"derivedFrom":subQ0}),makeQuery(id+"F0.imprint","IMPRINT",EDGE,{"disambiguationData":[TD([[subQ6,-1.0]])],"derivedFrom":subQ0}),makeQuery(id+"F0.imprint","IMPRINT",EDGE,{"disambiguationData":[TD([[subQ4,1.0]])],"derivedFrom":subQ0}),makeQuery(id+"F0.imprint","IMPRINT",EDGE,{"disambiguationData":[TD([[subQ3,1.0]])],"derivedFrom":subQ0}),makeQuery(id+"F0.imprint","IMPRINT",EDGE,{"disambiguationData":[TD([[subQ3,-1.0]])],"derivedFrom":subQ0}),makeQuery(id+"F0.imprint","IMPRINT",EDGE,{"disambiguationData":[TD([[subQ2,-1.0]])],"derivedFrom":subQ0}),makeQuery(id+"F0.imprint","IMPRINT",EDGE,{"disambiguationData":[TD([[subQ1,-1.0]])],"derivedFrom":subQ0})])],"isStart":false});}
            var Q2;
            {var subQ0=sQuery(id+"F0.wireOp",EDGE,"E1.top");Q2=makeQuery(id+"F3.opExtrude","CAP_EDGE",EDGE,{"disambiguationData":[OSD([subQ0]),TDD([makeQuery(id+"F0.imprint","IMPRINT",EDGE,{"disambiguationData":[TD([[makeQuery(id+"F0.imprint","INTERSECT",VERTEX,{"derivedFrom":[subQ0,sQuery(id+"F0.wireOp",EDGE,"E1.left")]}),-1.0]])],"derivedFrom":subQ0})])],"isStart":false});}
            var Q3;
            Q3=makeQuery(id+"F3.opExtrude","CAP_EDGE",EDGE,{"disambiguationData":[OSD([sQuery(id+"F0.wireOp",EDGE,"E1.left")])],"isStart":false});
            var Q4;
            Q4=makeQuery(id+"F3.opExtrude","SWEPT_EDGE",EDGE,{"disambiguationData":[OSD([sQuery(id+"F0.wireOp",EDGE,"E1.bottom"),sQuery(id+"F0.wireOp",EDGE,"E1.left")])]});
            var Q5;
            Q5=makeQuery(id+"F3.opExtrude","CAP_EDGE",EDGE,{"disambiguationData":[OSD([sQuery(id+"F0.wireOp",EDGE,"E0.sketch_text.stroke-116")])],"isStart":false});
            var Q6;
            Q6=makeQuery(id+"F3.opExtrude","CAP_EDGE",EDGE,{"disambiguationData":[OSD([sQuery(id+"F0.wireOp",EDGE,"E0.sketch_text.stroke-114")])],"isStart":false});
            var Q7;
            {var subQ0=sQuery(id+"F0.wireOp",EDGE,"E1.bottom");Q7=makeQuery(id+"F3.opExtrude","CAP_EDGE",EDGE,{"disambiguationData":[OSD([subQ0]),TDD([makeQuery(id+"F0.imprint","IMPRINT",EDGE,{"disambiguationData":[TD([[makeQuery(id+"F0.imprint","INTERSECT",VERTEX,{"derivedFrom":[sQuery(id+"F0.wireOp",EDGE,"E0.sketch_text.stroke-114"),subQ0]}),-1.0]])],"derivedFrom":subQ0})])],"isStart":false});}
            var Q8;
            {var subQ0=sQuery(id+"F0.wireOp",EDGE,"E1.bottom");var subQ1=makeQuery(id+"F0.imprint","INTERSECT",VERTEX,{"derivedFrom":[sQuery(id+"F0.wireOp",EDGE,"E0.sketch_text.stroke-193"),subQ0]});var subQ2=makeQuery(id+"F0.imprint","INTERSECT",VERTEX,{"derivedFrom":[sQuery(id+"F0.wireOp",EDGE,"E0.sketch_text.stroke-177"),subQ0]});var subQ3=makeQuery(id+"F0.imprint","INTERSECT",VERTEX,{"derivedFrom":[sQuery(id+"F0.wireOp",EDGE,"E0.sketch_text.stroke-181"),subQ0]});var subQ5=makeQuery(id+"F0.imprint","INTERSECT",VERTEX,{"derivedFrom":[sQuery(id+"F0.wireOp",EDGE,"E0.sketch_text.stroke-175"),subQ0]});var subQ6=makeQuery(id+"F0.imprint","INTERSECT",VERTEX,{"derivedFrom":[sQuery(id+"F0.wireOp",EDGE,"E0.sketch_text.stroke-159"),subQ0]});var subQ7=makeQuery(id+"F0.imprint","INTERSECT",VERTEX,{"derivedFrom":[sQuery(id+"F0.wireOp",EDGE,"E0.sketch_text.stroke-163"),subQ0]});var subQ9=makeQuery(id+"F0.imprint","INTERSECT",VERTEX,{"derivedFrom":[sQuery(id+"F0.wireOp",EDGE,"E0.sketch_text.stroke-157"),subQ0]});var subQ10=makeQuery(id+"F0.imprint","INTERSECT",VERTEX,{"derivedFrom":[sQuery(id+"F0.wireOp",EDGE,"E0.sketch_text.stroke-147"),subQ0]});Q8=makeQuery(id+"F3.opExtrude","CAP_EDGE",EDGE,{"disambiguationData":[OSD([subQ0]),TDD([makeQuery(id+"F0.imprint","IMPRINT",EDGE,{"disambiguationData":[TD([[subQ10,1.0]])],"derivedFrom":subQ0}),makeQuery(id+"F0.imprint","IMPRINT",EDGE,{"disambiguationData":[TD([[subQ10,-1.0]])],"derivedFrom":subQ0}),makeQuery(id+"F0.imprint","IMPRINT",EDGE,{"disambiguationData":[TD([[subQ9,-1.0]])],"derivedFrom":subQ0}),makeQuery(id+"F0.imprint","IMPRINT",EDGE,{"disambiguationData":[TD([[subQ7,1.0]])],"derivedFrom":subQ0}),makeQuery(id+"F0.imprint","IMPRINT",EDGE,{"disambiguationData":[TD([[subQ6,1.0]])],"derivedFrom":subQ0}),makeQuery(id+"F0.imprint","IMPRINT",EDGE,{"disambiguationData":[TD([[subQ6,-1.0]])],"derivedFrom":subQ0}),makeQuery(id+"F0.imprint","IMPRINT",EDGE,{"disambiguationData":[TD([[subQ5,-1.0]])],"derivedFrom":subQ0}),makeQuery(id+"F0.imprint","IMPRINT",EDGE,{"disambiguationData":[TD([[subQ3,1.0]])],"derivedFrom":subQ0}),makeQuery(id+"F0.imprint","IMPRINT",EDGE,{"disambiguationData":[TD([[subQ2,1.0]])],"derivedFrom":subQ0}),makeQuery(id+"F0.imprint","IMPRINT",EDGE,{"disambiguationData":[TD([[subQ2,-1.0]])],"derivedFrom":subQ0}),makeQuery(id+"F0.imprint","IMPRINT",EDGE,{"disambiguationData":[TD([[subQ1,-1.0]])],"derivedFrom":subQ0})])],"isStart":false});}
            var Q9;
            Q9=makeQuery(id+"F3.opExtrude","CAP_EDGE",EDGE,{"disambiguationData":[OSD([sQuery(id+"F0.wireOp",EDGE,"E1.right")])],"isStart":false});
            var Q10;
            Q10=makeQuery(id+"F3.opExtrude","SWEPT_EDGE",EDGE,{"disambiguationData":[OSD([sQuery(id+"F0.wireOp",EDGE,"E1.bottom"),sQuery(id+"F0.wireOp",EDGE,"E1.right")])]});
            fillet(context, id + "F4", {"entities" : qUnion([Q0, Q1, Q2, Q3, Q4, Q5, Q6, Q7, Q8, Q9, Q10]), "tangentPropagation" : true, "radius" : 1 * mm, "defaultsChanged" : false, "vertexSettings" : [], "allowEdgeOverflow" : false});
        }
    });
